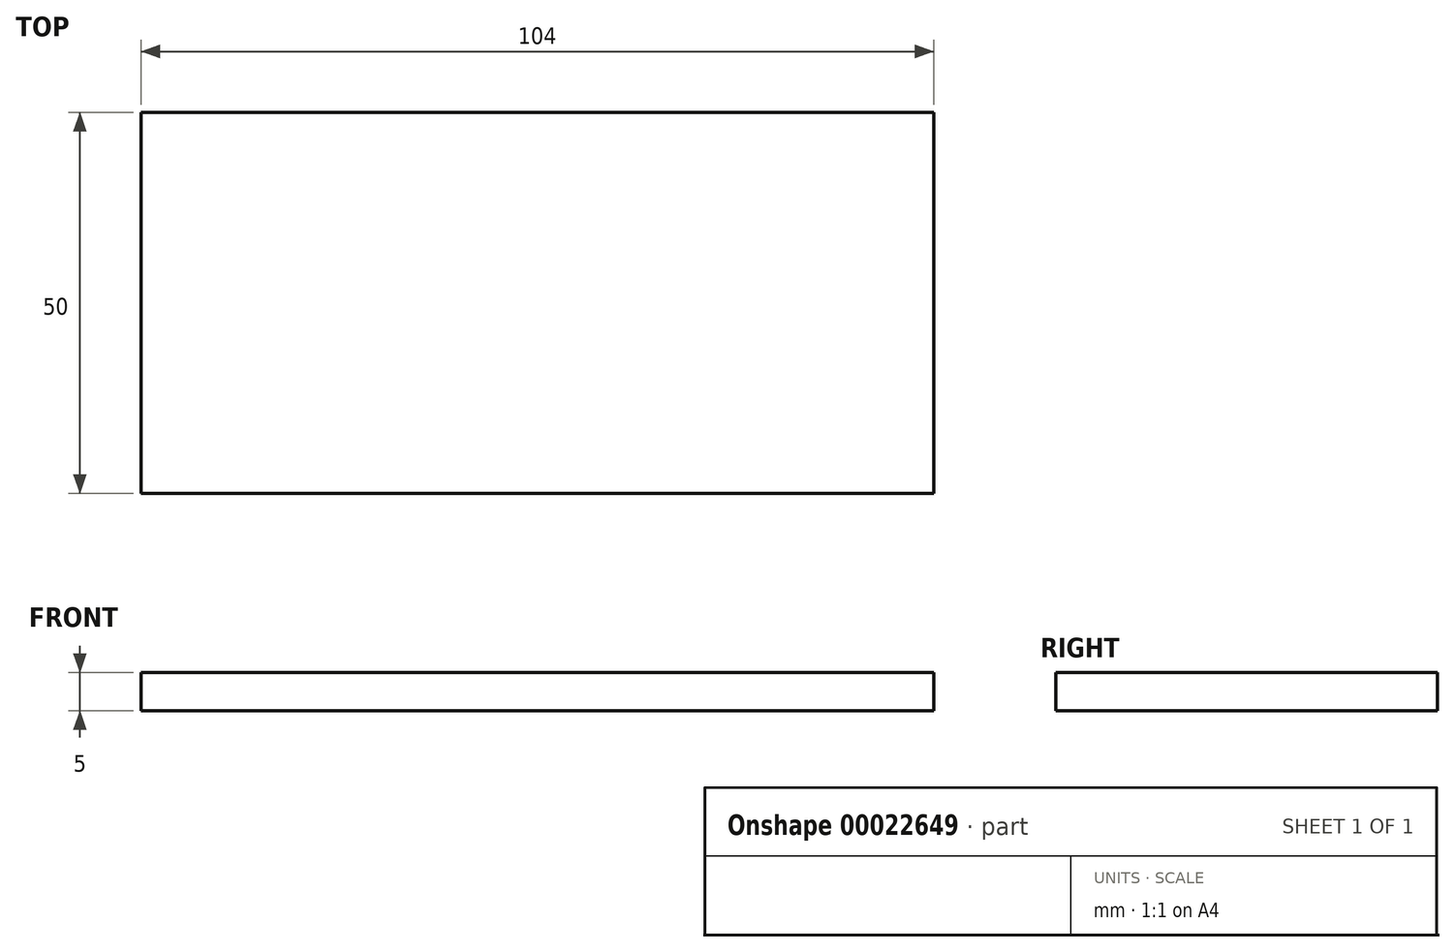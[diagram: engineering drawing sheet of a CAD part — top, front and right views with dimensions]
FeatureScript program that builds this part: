
annotation { "Feature Type Name" : "Feature", "Feature Type Description" : "" }
export const myFeature = defineFeature(function(context is Context, id is Id, definition is map)
    precondition{}
    {
        {
            var Q0;
            Q0=qCreatedBy(makeId("Top.planeOp"),FACE);
            var sketch = newSketch(context, id + "F0", { "sketchPlane" : qUnion([Q0])});
            skLineSegment(sketch, "E0.bottom", {"start": v(-52, 25) * mm, "end": v(52, 25) * mm});
            skLineSegment(sketch, "E0.top", {"start": v(-52, -25) * mm, "end": v(52, -25) * mm});
            skLineSegment(sketch, "E0.left", {"start": v(-52, 25) * mm, "end": v(-52, -25) * mm});
            skLineSegment(sketch, "E0.right", {"start": v(52, 25) * mm, "end": v(52, -25) * mm});
            skSolve(sketch);
        }
        {
            var Q0;
            Q0=makeQuery(id+"F0.imprint","IMPRINT",FACE,{"disambiguationData":[TD([[makeQuery(id+"F0.imprint","IMPRINT",EDGE,{"derivedFrom":sQuery(id+"F0.wireOp",EDGE,"E0.bottom")}),-1.0]])]});
            extrude(context, id + "F1", {"entities" : qUnion([Q0]), "depth" : 5 * mm});
        }
    });
